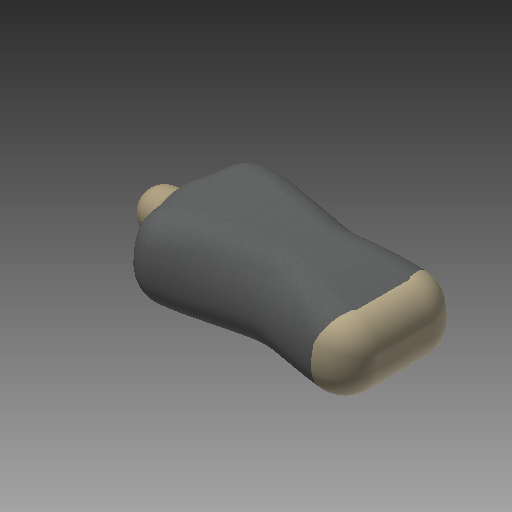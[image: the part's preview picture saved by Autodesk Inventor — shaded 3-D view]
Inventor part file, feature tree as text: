
AUTODESK INVENTOR PART (.ipt)
format: ipt  version: 2022 (Build 260153000, 153)  size: 588,288 bytes
history: native  units: mm (DEFAULTED — no unit token found)
features: other x6, plane x4, sketch x4, revolve x2, extrude x2, fillet x2
ambient origin geometry x8: Origin, YZ Plane, XZ Plane, XY Plane, X Axis, Y Axis, Z Axis, Center Point
bodies: Solid1 (feature_tree)
feature tree (20):
  other  "iMan - 2D BODY"
  revolve  "Revolution1"  [1 undecoded]
  extrude  "Extrusion3"  Depth=358.14mm
  plane  "Work Plane6"
  extrude  "Extrusion2"  Depth=13.613568mm
  plane  "Work Plane7"
  revolve  "Revolution3"  [1 undecoded]
  fillet  "Fillet1"  [1 undecoded]
  fillet  "Fillet2"  Radius=46.641715mm
  plane  "Work Plane2"
  plane  "Work Plane3"
  other  "Work Axis1"
  other  "Work Axis3"
  other  "Work Axis4"
  other  "Work Point5"
  other  "Work Point6"
  sketch  "Sketch1"  dims[d1=10.0mm d28=94.17558mm]
  sketch  "Sketch8"  dims[d29=222.254369mm d30=358.14mm]
  sketch  "Sketch9"  dims[d31=17.78mm d33=13.613568mm]
  sketch  "Sketch11"  dims[d35=97.17024mm d36=404.876mm d37=90.0deg d42=46.641715mm d62=599.79814mm d63=181.1528mm d64=-181.1528mm d70=90.408557mm d72=0.0mm d73=120.353938mm d86=26.5557mm d87=0.0mm d88=180.0deg d89=0.0mm d101=181.64048mm d102=188.35116mm d103=26.5557mm d104=0.0mm d130=24.29256mm d131=45.41012mm d132=7.62mm d133=10.16mm d134=37.670232mm d135=150.680928mm d136=145.312384mm d137=90.0deg d138=179.939442mm d139=2.54mm d140=17.78mm]
note: 3 required parameter values undecoded (feature->parameter linkage not recoverable at this tier; creation-order binding heuristic only, values carry confidence <= 0.55)